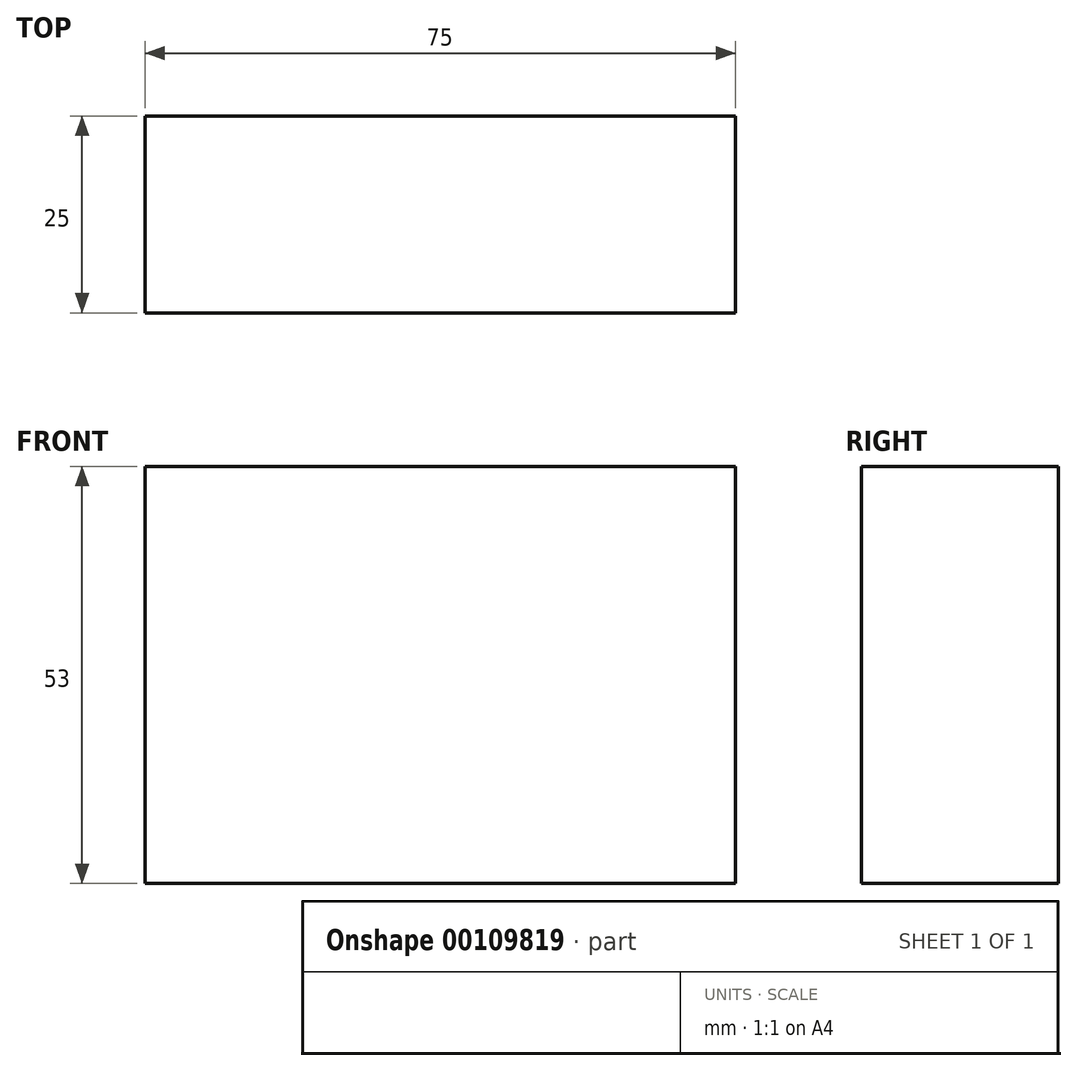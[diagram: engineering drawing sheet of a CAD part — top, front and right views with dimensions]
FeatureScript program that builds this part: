
annotation { "Feature Type Name" : "Feature", "Feature Type Description" : "" }
export const myFeature = defineFeature(function(context is Context, id is Id, definition is map)
    precondition{}
    {
        {
            var Q0;
            Q0=qCreatedBy(makeId("Front.planeOp"),FACE);
            var sketch = newSketch(context, id + "F0", { "sketchPlane" : qUnion([Q0])});
            skLineSegment(sketch, "E0.bottom", {"start": v(37.5, -26.5) * mm, "end": v(-37.5, -26.5) * mm});
            skLineSegment(sketch, "E0.top", {"start": v(37.5, 26.5) * mm, "end": v(-37.5, 26.5) * mm});
            skLineSegment(sketch, "E0.left", {"start": v(37.5, -26.5) * mm, "end": v(37.5, 26.5) * mm});
            skLineSegment(sketch, "E0.right", {"start": v(-37.5, -26.5) * mm, "end": v(-37.5, 26.5) * mm});
            skPoint(sketch, "E0.middle", {"position": v(0, 0) * mm});
            skSolve(sketch);
        }
        {
            var Q0;
            Q0 = qSketchRegion(id + "F0", true);
            extrude(context, id + "F1", {"entities" : qUnion([Q0]), "depth" : 25 * mm});
        }
    });
